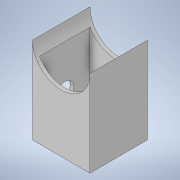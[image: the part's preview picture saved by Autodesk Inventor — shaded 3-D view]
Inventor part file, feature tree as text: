
AUTODESK INVENTOR PART (.ipt)
format: ipt  version: 2021 (Build 250183000, 183)  size: 119,808 bytes
history: native  units: in
note: dims shown in document units (in); Inventor stores cm internally (conversion verified against a paired STEP export)
features: extrude x3, sketch x3
ambient origin geometry x8: Origin, YZ Plane, XZ Plane, XY Plane, X Axis, Y Axis, Z Axis, Center Point
bodies: Body1 (feature_tree)
feature tree (6):
  extrude  "Extrusion2"  Depth=1.0in
  extrude  "Extrusion4"  Depth=0.9375in
  extrude  "Extrusion6"  Depth=0.875in
  sketch  "Sketch3"  dims[d4=1.0in d5=1.0in]
  sketch  "Sketch5"  dims[d6=0.0625in d7=0.9375in]
  sketch  "Sketch8"  dims[d8=0.875in d9=0.875in d10=1.5in d11=0.0in d16=1.0in d17=0.0in d22=0.313in d23=0.5in d24=0.0in]
